# Revit family: Franke_Flavor_Station_FS3-A600_FM_EC_A600_FM_CM_A800_FM_EC
name_source: partatom
category: Sonderausstattung
revit_build: Autodesk Revit 2015 (Build: 20140606_1530(x64)
units: mm (PartAtom-declared; Revit-internal decimal feet)

## types (2) — shared parameters
Anzahl der Nullleiter = 1
Anzahl der Schutzleiter = 1
Anzahl von Polen = 1
Aufstellgewicht = 17 kg
Bauelement = Beistellgerät Flavor Station
Baugruppenkennzeichen = Beistellgerät Flavor Station
Beschreibung = Beistellgerät Flavor Station ermöglicht die vollautomatisierte und konstant dosierte Zuführung von Sirups
Breite = 200 mm  [stored 0.656168 ft]
Energieverlust nach DIN18873 = k.A.
Hersteller = Franke
Höhe = 544 mm
Kapazität = max. 3 Flaschen
Leistung = 50 W
Modell = 410888 - Flavor Station FS3-A600 FM EC, A600 FM CM, A800 FM EC
Netzfrequenz = 50 Hz
Netzfrequenz alternativ = 60 Hz
Sicherung = 10 A
Spannung = 230 V
Tiefe = 452 mm  [stored 1.48294 ft]
URL = http://www.franke.com
zero-valued in all types: Kosten

## per-type parameters (varying)
| type | Abdeckung |
| Flavor Station FS3-A600 FM EC,A600 FM CM,A800 FM EC(230V/black line/EU) | Franke Black |
| Flavor Station FS3-A600 FM EC,A600 FM CM,A800 FM EC(230V/anthrazit/EU) | Franke Anthrazit |

note: [stored X ft] marks values corroborated as IEEE doubles in the binary element streams (Revit-internal decimal feet)
